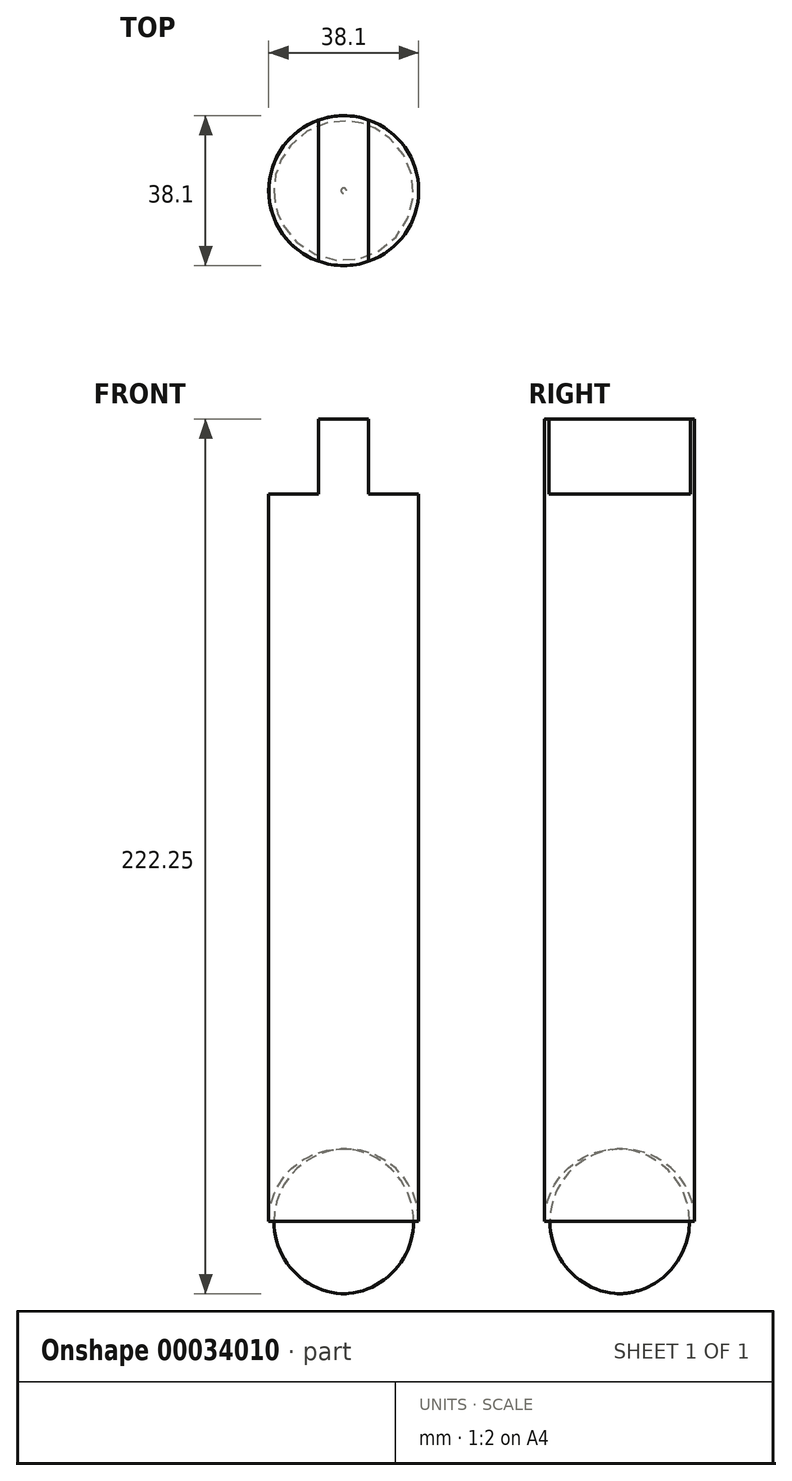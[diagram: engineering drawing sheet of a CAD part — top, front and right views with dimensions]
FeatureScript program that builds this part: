
annotation { "Feature Type Name" : "Feature", "Feature Type Description" : "" }
export const myFeature = defineFeature(function(context is Context, id is Id, definition is map)
    precondition{}
    {
        {
            var Q0;
            Q0=qCreatedBy(makeId("Top.planeOp"),FACE);
            var sketch = newSketch(context, id + "F0", { "sketchPlane" : qUnion([Q0])});
            skCircle(sketch, "E0", {"center": v(0, 0) * mm, "radius": 19.05 * mm});
            skSolve(sketch);
        }
        {
            var Q0;
            Q0 = qSketchRegion(id + "F0", true);
            extrude(context, id + "F1", {"entities" : qUnion([Q0]), "depth" : 203.2 * mm});
        }
        {
            var Q0;
            Q0=makeQuery(id+"F1.opExtrude","CAP_FACE",FACE,{"disambiguationData":[OSD([sQuery(id+"F0.wireOp",EDGE,"E0")])],"isStart":false});
            var sketch = newSketch(context, id + "F2", { "sketchPlane" : qUnion([Q0])});
            skLineSegment(sketch, "E1.bottom", {"start": v(-6.35, -21.44) * mm, "end": v(6.35, -21.44) * mm});
            skLineSegment(sketch, "E1.top", {"start": v(-6.35, 21.25) * mm, "end": v(6.35, 21.25) * mm});
            skLineSegment(sketch, "E1.left", {"start": v(-6.35, -21.44) * mm, "end": v(-6.35, 21.25) * mm});
            skLineSegment(sketch, "E1.right", {"start": v(6.35, -21.44) * mm, "end": v(6.35, 21.25) * mm});
            skSolve(sketch);
        }
        {
            var Q0;
            {var subQ0=makeQuery(id+"F1.opExtrude","CAP_EDGE",EDGE,{"disambiguationData":[OSD([sQuery(id+"F0.wireOp",EDGE,"E0")])],"isStart":false});var subQ3=sQuery(id+"F2.wireOp",EDGE,"E1.left");var subQ6=makeQuery(id+"F2.imprint","INTERSECT",VERTEX,{"disambiguationData":[OD(0.0)],"derivedFrom":[subQ0,subQ3]});Q0=makeQuery(id+"F2.imprint","IMPRINT",FACE,{"disambiguationData":[TD([[makeQuery(id+"F2.imprint","IMPRINT",EDGE,{"disambiguationData":[TD([[subQ6,-1.0]])],"derivedFrom":subQ3}),-1.0]])]});}
            var Q1;
            Q1=makeQuery(id+"F1.opExtrude","CAP_FACE",FACE,{"disambiguationData":[OSD([sQuery(id+"F0.wireOp",EDGE,"E0")])],"isStart":true});
            extrude(context, id + "F3", {"entities" : qUnion([Q0, Q1]), "operationType" : NewBodyOperationType.ADD, "depth" : 19.05 * mm});
        }
        {
            var Q0;
            Q0=makeQuery(id+"F1.opExtrude","CAP_FACE",FACE,{"disambiguationData":[OSD([sQuery(id+"F0.wireOp",EDGE,"E0")])],"isStart":true});
            fillet(context, id + "F4", {"entities" : qUnion([Q0]), "radius" : 18.4 * mm, "tangentPropagation" : true, "allowEdgeOverflow" : false});
        }
    });
